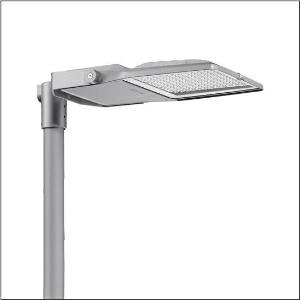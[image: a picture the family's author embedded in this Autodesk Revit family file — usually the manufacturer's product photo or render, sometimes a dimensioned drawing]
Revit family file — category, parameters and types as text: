
# Revit family: floodlight_fl_21_midi___pl61_5xa7786f2c3a_551f
name_source: partatom
category: Lighting Fixtures
units: mm (PartAtom-declared; Revit-internal decimal feet)

## family parameters
Cut with Voids When Loaded = No
Host = Face
Light Source = No
Part Type = Normal
Room Calculation Point = No
Round Connector Dimension = Use Diameter
Shared = No

## types (1)
- --- (1 x LED, 35100 lm, 271.6 W, 3000K)
    Apparent Load = 272 VA
    CIE Flux Codes = 33 65 98 100 100
    Color Rendering = 70
    Color Temperature = 3000K
    Default Elevation = 1800 mm
    Description = Floodlight FL 21 midi, floodlight, primary light control with lens, of PMMA, primary optical cover: protective disc, of toughened safety glass, transparent, light distribution: PL61, light emission: direct distribution, installation type: surface-mounted, LED, High Power LED, rated luminous flux: 35.100lm, luminous efficacy: 129lm/W, light colour: 730, colour temperature: 3000K, control gear: ECG Smart Interface, control: flexible luminous flux parameterisation, time-dependent luminous flux control, constant luminous flux control, overheat protection, presetting dimming logarithmic, with terminal, 6-pole, mains connection: 220..240V, AC, 50/60Hz, start of lifetime: 272W, end of service life: 287W, reduction: 123W, luminaire housing, of diecast aluminium, powder-coated, Siteco® metallic grey (DB 702S), corrosivity category C5 mid according to DIN EN ISO 12944, sealing non-destructively replaceable, please order mast flange separately, mast bracket, of steel, galvanised, powder-coated, Siteco® metallic grey (DB 702S), Smart Interface below and above, protection rating (complete): IP66, insulation class (complete): insulation class II (safety insulation), certification: CE, protection symbol: D, impact resistance: IK08, permissible operating ambient temperature: -40..+40°C, permissible operating ambient temperature for outdoor applications: -40..+50°C, standard: DIN EN 12944, LABS conformity tested according to VDMA 24364:2018-05, packaging unit: 1 piece

Light Distribution: PL61
    Height = 76 mm
    Lamp = 1 x LED
    Lamp Light Flux = 35100 lm
    Lamp Power = 271.6 W
    Lamp count = 1
    Length = 657 mm
    Luminous efficacy = 129 lm/W
    Manufacturer = Siteco
    ModVariant = No
    Model = 5XA7786F2C3A
    Number of Poles = 1
    OnlyDefault = Yes
    Power Factor = 1
    Product Name = Floodlight FL 21 midi | PL61
    Product group = floodlight | pylon annexe
    ProductGroupID = 6200
    Protection Class = Protection class II
    Protection Degree = IP 66
    RLX_Detail_Level = 1
    RLX_Emergency_Light_Flux = 0 lm
    RLX_Emergency_Type = 0
    RLX_Emergency_Type_DB = No
    RlxData = <blob elided: 153609 chars, md5=ef48e24f>
    Socket = socket
    Standby Power = 0 W
    System Light Flux = 35100 lm
    System Power = 272 W
    Type Comments = factory setting: luminous flux: 100 % | dim-lin: 254 | 620 mA
    Type Image = l_1007123.jpg
    URL = http://relux.com
    VarID = @adj_146569
    Voltage = 0 V
    Weight = 0.00 kg
    Width = 442 mm

## geometry (parser evidence)
native form markers: Blend x4, Sweep x15
no freeform markers — native parametric forms only
